# Revit family: Grab_Bar-Grohe-Essentials-40794001
name_source: partatom
category: Specialty Equipment
units: mm (PartAtom-declared; Revit-internal decimal feet)

## family parameters
Cut with Voids When Loaded = No
Host = Face
OmniClass Number = 23.40.20.21.27
OmniClass Title = Towel Bars
Part Type = Normal
Room Calculation Point = No
Round Connector Dimension = Use Diameter
Shared = Yes

## types (1)
- 40794001
    Assembly Code = C1030200
    Default Elevation = 35 3/8"
    Description = Essentials 24" Grab Bar
    Height = 2 1/4"
    Installation Type = Wall Mounted
    Length = 23 5/8"
    Manufacturer = GROHE
    Material = Metal-Grohe-000-Starlight_Chrome
    Model = 40794001
    Price = Prices may vary. Please consult Manufacturer Representative for most up-to-date price list.
    Product Documentation Link = https://americanstandard.box.com
    Product Page URL = https://www.grohe.ca
    Revised Date = 05/10/2021
    URL = https://www.grohe.ca
    Warranty Information = Limited Lifetime Warranty
    Width = 3 21/32"

## geometry (parser evidence)
native form markers: Sweep x3
no freeform markers — native parametric forms only
